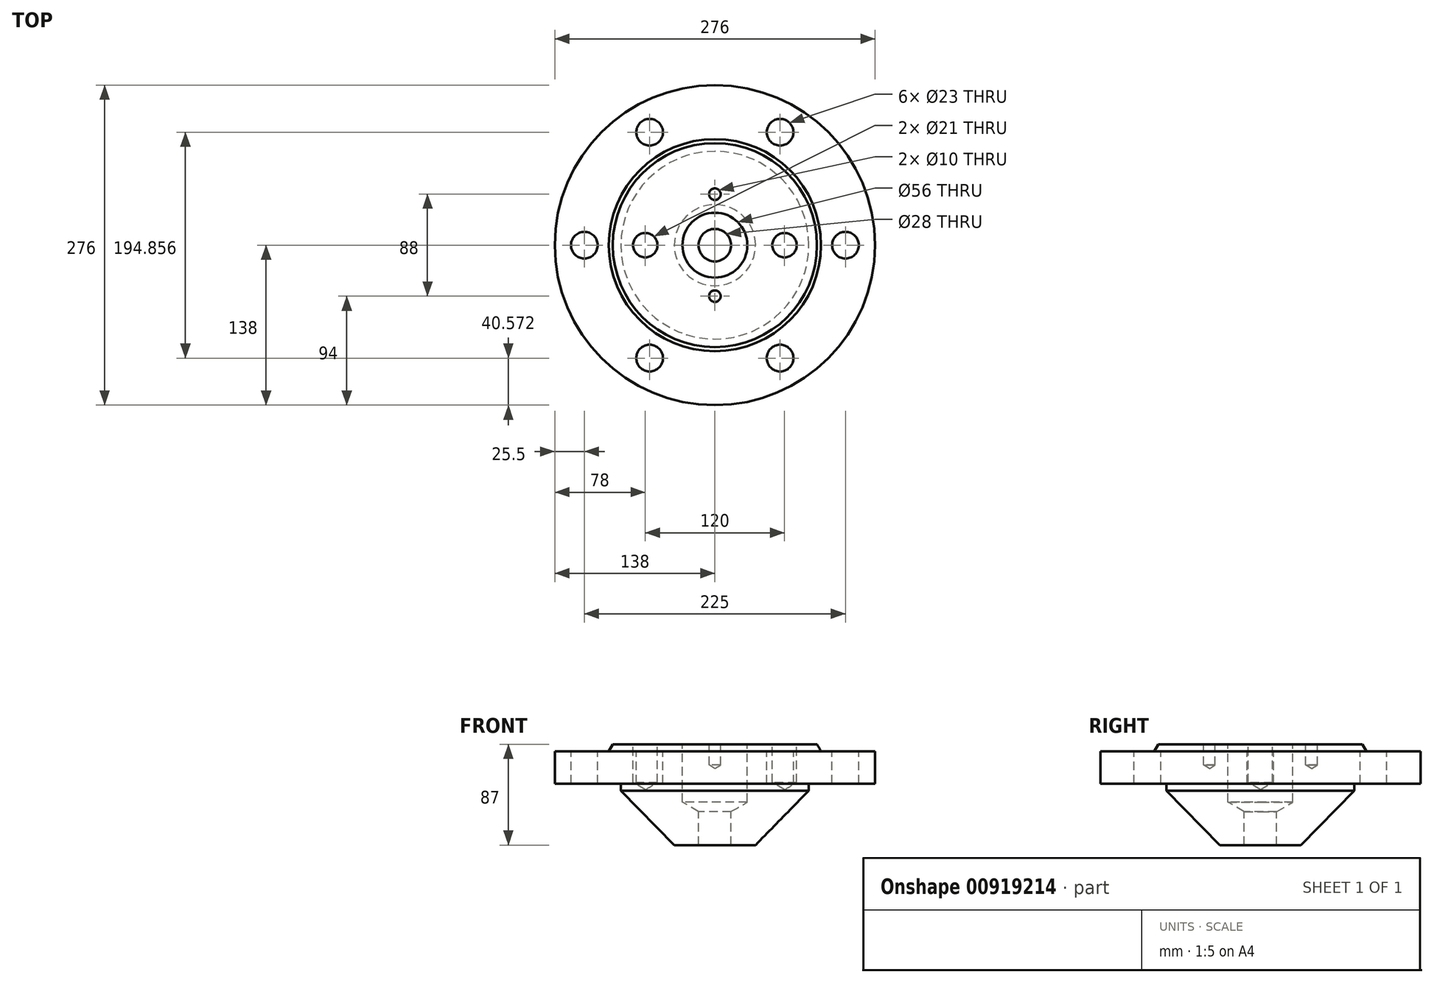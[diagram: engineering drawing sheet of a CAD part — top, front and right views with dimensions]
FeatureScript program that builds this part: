
annotation { "Feature Type Name" : "Feature", "Feature Type Description" : "" }
export const myFeature = defineFeature(function(context is Context, id is Id, definition is map)
    precondition{}
    {
        {
            var Q0;
            Q0=qCreatedBy(makeId("Front.planeOp"),FACE);
            var sketch = newSketch(context, id + "F0", { "sketchPlane" : qUnion([Q0])});
            skLineSegment(sketch, "E0", {"start": v(0, 12.04) * mm, "end": v(-28, 12.04) * mm});
            skLineSegment(sketch, "E1", {"start": v(-28, 12.04) * mm, "end": v(-28, -37.96) * mm});
            skLineSegment(sketch, "E2", {"start": v(-28, 12.04) * mm, "end": v(-88, 12.04) * mm});
            skLineSegment(sketch, "E3", {"start": v(-88, 12.04) * mm, "end": v(-91.46, 6.04) * mm});
            skLineSegment(sketch, "E4", {"start": v(-91.46, 6.04) * mm, "end": v(-138, 6.04) * mm});
            skLineSegment(sketch, "E5", {"start": v(-138, 6.04) * mm, "end": v(-138, -21.96) * mm});
            skLineSegment(sketch, "E6", {"start": v(-138, -21.96) * mm, "end": v(-81, -21.96) * mm});
            skLineSegment(sketch, "E7", {"start": v(-81, -21.96) * mm, "end": v(-81, -27.96) * mm});
            skLineSegment(sketch, "E8", {"start": v(0, -74.96) * mm, "end": v(-35, -74.96) * mm});
            skLineSegment(sketch, "E9", {"start": v(-35, -74.96) * mm, "end": v(-81, -27.96) * mm});
            skLineSegment(sketch, "E10", {"start": v(0, 75.02) * mm, "end": v(0, -110.71) * mm, "construction": true});
            skLineSegment(sketch, "E11", {"start": v(-28, -37.96) * mm, "end": v(-14, -46.04) * mm});
            skLineSegment(sketch, "E12", {"start": v(-14, -74.96) * mm, "end": v(-14, -46.04) * mm});
            skSolve(sketch);
        }
        {
            var Q0;
            Q0=makeQuery(id+"F0.imprint","IMPRINT",FACE,{"disambiguationData":[TD([[makeQuery(id+"F0.imprint","IMPRINT",EDGE,{"derivedFrom":sQuery(id+"F0.wireOp",EDGE,"E1")}),-1.0]])]});
            var Q1;
            Q1=sQuery(id+"F0.wireOp",EDGE,"E10");
            revolve(context, id + "F1", {"surfaceOperationType" : NewSurfaceOperationType.NEW, "entities" : qUnion([Q0]), "axis" : qUnion([Q1]), "revolveType" : RevolveType.FULL});
        }
        {
            var Q0;
            Q0=makeQuery(id+"F1.opRevolve","SWEPT_FACE",FACE,{"disambiguationData":[OSD([sQuery(id+"F0.wireOp",EDGE,"E4")])]});
            var sketch = newSketch(context, id + "F2", { "sketchPlane" : qUnion([Q0])});
            skCircle(sketch, "E13", {"center": v(0, 0) * mm, "radius": 112.5 * mm, "construction": true});
            skLineSegment(sketch, "E14", {"start": v(171.08, 0) * mm, "end": v(-203.7, 0) * mm, "construction": true});
            skCircle(sketch, "E15", {"center": v(-112.5, 0) * mm, "radius": 11.5 * mm});
            skLineSegment(sketch, "E16", {"start": v(0, 0) * mm, "end": v(117.79, -204.02) * mm, "construction": true});
            skLineSegment(sketch, "E17", {"start": v(0, 0) * mm, "end": v(-98.7, -170.97) * mm, "construction": true});
            skLineSegment(sketch, "E18", {"start": v(0, 0) * mm, "end": v(-89.54, 155.08) * mm, "construction": true});
            skLineSegment(sketch, "E19", {"start": v(0, 0) * mm, "end": v(75.32, 130.46) * mm, "construction": true});
            skCircle(sketch, "E20", {"center": v(-56.25, 97.43) * mm, "radius": 11.5 * mm});
            skCircle(sketch, "E21", {"center": v(56.25, 97.43) * mm, "radius": 11.5 * mm});
            skCircle(sketch, "E22", {"center": v(112.5, 0) * mm, "radius": 11.5 * mm});
            skCircle(sketch, "E23", {"center": v(56.25, -97.43) * mm, "radius": 11.5 * mm});
            skCircle(sketch, "E24", {"center": v(-56.25, -97.43) * mm, "radius": 11.5 * mm});
            skSolve(sketch);
        }
        {
            var Q0;
            Q0=makeQuery(id+"F2.imprint","IMPRINT",FACE,{"disambiguationData":[TD([[makeQuery(id+"F2.imprint","IMPRINT",EDGE,{"derivedFrom":sQuery(id+"F2.wireOp",EDGE,"E15")}),1.0]])]});
            extrude(context, id + "F3", {"entities" : qUnion([Q0]), "operationType" : NewBodyOperationType.REMOVE, "endBound" : BoundingType.THROUGH_ALL, "oppositeDirection" : true, "depth" : 25 * mm, "offsetDistance" : 25 * mm});
        }
        {
            var Q0;
            Q0=makeQuery(id+"F2.imprint","IMPRINT",FACE,{"disambiguationData":[TD([[makeQuery(id+"F2.imprint","IMPRINT",EDGE,{"derivedFrom":sQuery(id+"F2.wireOp",EDGE,"E20")}),1.0]])]});
            var Q1;
            Q1=makeQuery(id+"F2.imprint","IMPRINT",FACE,{"disambiguationData":[TD([[makeQuery(id+"F2.imprint","IMPRINT",EDGE,{"derivedFrom":sQuery(id+"F2.wireOp",EDGE,"E21")}),1.0]])]});
            var Q2;
            Q2=makeQuery(id+"F2.imprint","IMPRINT",FACE,{"disambiguationData":[TD([[makeQuery(id+"F2.imprint","IMPRINT",EDGE,{"derivedFrom":sQuery(id+"F2.wireOp",EDGE,"E22")}),1.0]])]});
            var Q3;
            Q3=makeQuery(id+"F2.imprint","IMPRINT",FACE,{"disambiguationData":[TD([[makeQuery(id+"F2.imprint","IMPRINT",EDGE,{"derivedFrom":sQuery(id+"F2.wireOp",EDGE,"E23")}),1.0]])]});
            var Q4;
            Q4=makeQuery(id+"F2.imprint","IMPRINT",FACE,{"disambiguationData":[TD([[makeQuery(id+"F2.imprint","IMPRINT",EDGE,{"derivedFrom":sQuery(id+"F2.wireOp",EDGE,"E24")}),1.0]])]});
            extrude(context, id + "F4", {"entities" : qUnion([Q0, Q1, Q2, Q3, Q4]), "operationType" : NewBodyOperationType.REMOVE, "endBound" : BoundingType.UP_TO_NEXT, "oppositeDirection" : true, "depth" : 25 * mm, "offsetDistance" : 25 * mm});
        }
        {
            var Q0;
            Q0=makeQuery(id+"F1.opRevolve","SWEPT_FACE",FACE,{"disambiguationData":[OSD([sQuery(id+"F0.wireOp",EDGE,"E2")])]});
            var sketch = newSketch(context, id + "F5", { "sketchPlane" : qUnion([Q0])});
            skCircle(sketch, "E25", {"center": v(0, 0) * mm, "radius": 60 * mm, "construction": true});
            skCircle(sketch, "E26", {"center": v(-60, 0) * mm, "radius": 10.5 * mm});
            skCircle(sketch, "E27", {"center": v(60, 0) * mm, "radius": 10.5 * mm});
            skCircle(sketch, "E28", {"center": v(0, 0) * mm, "radius": 44 * mm, "construction": true});
            skLineSegment(sketch, "E29", {"start": v(0, 135.75) * mm, "end": v(0, -100.25) * mm, "construction": true});
            skCircle(sketch, "E30", {"center": v(0, 44) * mm, "radius": 5 * mm});
            skCircle(sketch, "E31", {"center": v(0, -44) * mm, "radius": 5 * mm});
            skSolve(sketch);
        }
        {
            var Q0;
            Q0=sQuery(id+"F5.wireOp",VERTEX,"E26.center");
            var Q1;
            Q1=sQuery(id+"F5.wireOp",VERTEX,"E27.center");
            var Q2;
            Q2=makeQuery(id+"F1.opRevolve","SWEPT_BODY",BODY,{"disambiguationData":[OSD([sQuery(id+"F0.wireOp",EDGE,"E1"),sQuery(id+"F0.wireOp",EDGE,"E2"),sQuery(id+"F0.wireOp",EDGE,"E3"),sQuery(id+"F0.wireOp",EDGE,"E4"),sQuery(id+"F0.wireOp",EDGE,"E5"),sQuery(id+"F0.wireOp",EDGE,"E6"),sQuery(id+"F0.wireOp",EDGE,"E7"),sQuery(id+"F0.wireOp",EDGE,"E8"),sQuery(id+"F0.wireOp",EDGE,"E9"),sQuery(id+"F0.wireOp",EDGE,"E11"),sQuery(id+"F0.wireOp",EDGE,"E12")])]});
            hole(context, id + "F6", {"style" : HoleStyle.SIMPLE, "endStyle" : HoleEndStyle.BLIND, "holeDiameter" : 21 * mm, "majorDiameter" : 5 * mm, "holeDepth" : 33 * mm, "isTappedThrough" : true, "tappedDepth" : 12 * mm, "tapClearance" : 3, "locations" : qUnion([Q0, Q1]), "scope" : qUnion([Q2])});
        }
        {
            var Q0;
            Q0=sQuery(id+"F5.wireOp",VERTEX,"E30.center");
            var Q1;
            Q1=sQuery(id+"F5.wireOp",VERTEX,"E31.center");
            var Q2;
            Q2=makeQuery(id+"F1.opRevolve","SWEPT_BODY",BODY,{"disambiguationData":[OSD([sQuery(id+"F0.wireOp",EDGE,"E1"),sQuery(id+"F0.wireOp",EDGE,"E2"),sQuery(id+"F0.wireOp",EDGE,"E3"),sQuery(id+"F0.wireOp",EDGE,"E4"),sQuery(id+"F0.wireOp",EDGE,"E5"),sQuery(id+"F0.wireOp",EDGE,"E6"),sQuery(id+"F0.wireOp",EDGE,"E7"),sQuery(id+"F0.wireOp",EDGE,"E8"),sQuery(id+"F0.wireOp",EDGE,"E9"),sQuery(id+"F0.wireOp",EDGE,"E11"),sQuery(id+"F0.wireOp",EDGE,"E12")])]});
            hole(context, id + "F7", {"style" : HoleStyle.SIMPLE, "endStyle" : HoleEndStyle.BLIND, "holeDiameter" : 10 * mm, "majorDiameter" : 5 * mm, "holeDepth" : 18 * mm, "isTappedThrough" : true, "tappedDepth" : 12 * mm, "tapClearance" : 3, "locations" : qUnion([Q0, Q1]), "scope" : qUnion([Q2])});
        }
    });
